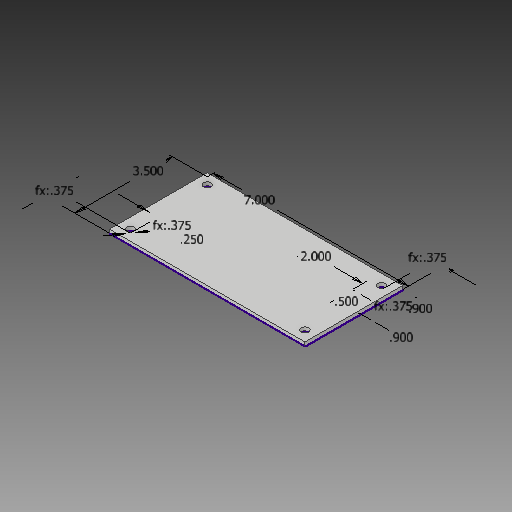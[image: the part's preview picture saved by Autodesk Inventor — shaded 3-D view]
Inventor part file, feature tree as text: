
AUTODESK INVENTOR PART (.ipt)
format: ipt  version: 2018 (Build 220112000, 112)  size: 118,784 bytes
history: native  units: in
note: dims shown in document units (in); Inventor stores cm internally (conversion verified against a paired STEP export)
features: sketch x3, extrude x2, hole x2
ambient origin geometry x8: Origin, YZ Plane, XZ Plane, XY Plane, X Axis, Y Axis, Z Axis, Center Point
bodies: Solid1 (feature_tree)
feature tree (7):
  sketch  "Sketch1"  dims[d0=7.0in d1=3.5in]
  extrude  "Extrusion1"  Depth=3.5in
  extrude  "Extrusion2"  Depth=0.9in
  sketch  "Sketch2"  dims[d2=0.9in d3=0.9in]
  hole  "Hole3"  [1 undecoded]
  sketch  "Sketch4"  dims[d4=0.5in d5=2.0in d6=0.125in d7=0.0in d8=0.6in d9=0.0in d10=0.375in d11=0.375in d12=0.375in d13=0.375in d14=0.25in d15=0.375in d16=0.375in d24=0.266in d25=0.75in d26=0.375in d27=0.25in d28=0.5635in d29=1.0in d30=0.0in]
  hole  "Hole2"  [1 undecoded]
note: 2 required parameter values undecoded (feature->parameter linkage not recoverable at this tier; creation-order binding heuristic only, values carry confidence <= 0.55)
